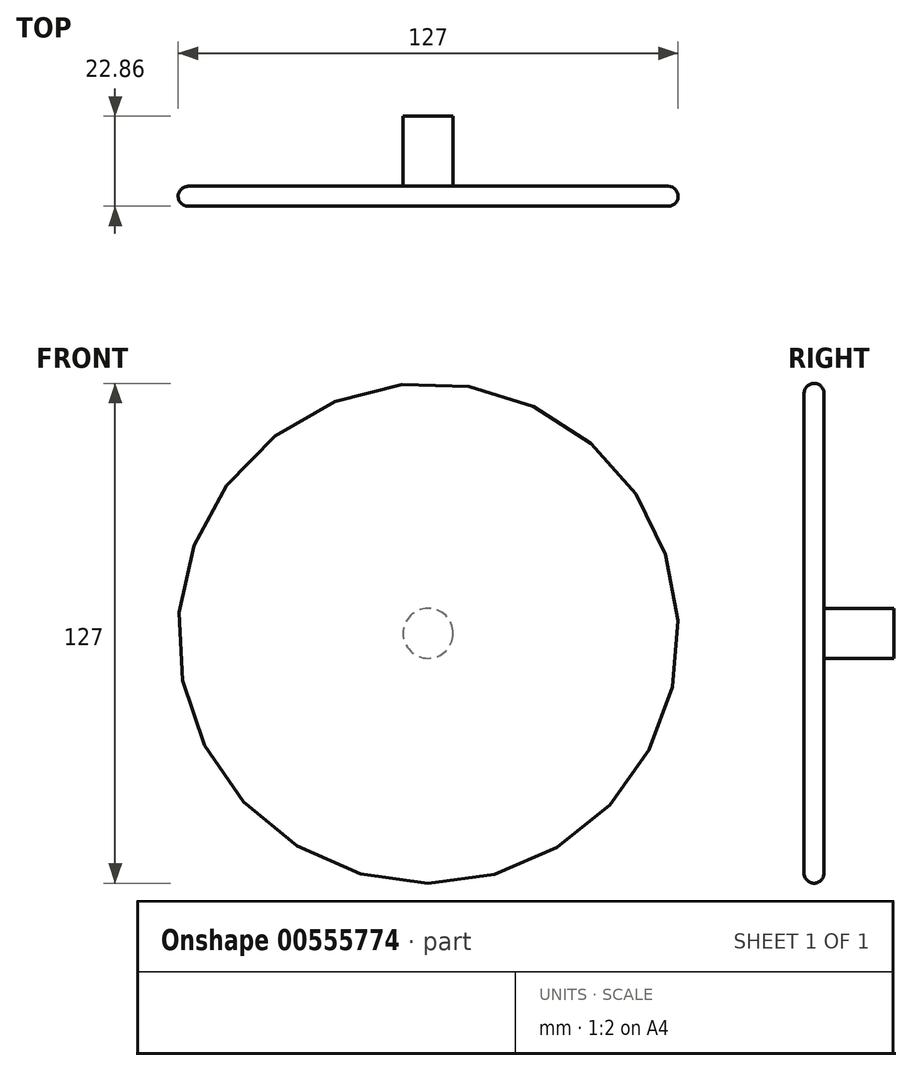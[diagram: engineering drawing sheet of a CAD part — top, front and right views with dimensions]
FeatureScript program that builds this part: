
annotation { "Feature Type Name" : "Feature", "Feature Type Description" : "" }
export const myFeature = defineFeature(function(context is Context, id is Id, definition is map)
    precondition{}
    {
        {
            var Q0;
            Q0=qCreatedBy(makeId("Front.planeOp"),FACE);
            var sketch = newSketch(context, id + "F0", { "sketchPlane" : qUnion([Q0])});
            skCircle(sketch, "E0", {"center": v(0, 0) * mm, "radius": 6.35 * mm});
            skSolve(sketch);
        }
        {
            var Q0;
            Q0=makeQuery(id+"F0.imprint","IMPRINT",FACE,{"disambiguationData":[TD([[makeQuery(id+"F0.imprint","IMPRINT",EDGE,{"derivedFrom":sQuery(id+"F0.wireOp",EDGE,"E0")}),1.0]])]});
            extrude(context, id + "F1", {"entities" : qUnion([Q0]), "depth" : 25.4 * mm, "offsetDistance" : 25.4 * mm});
        }
        {
            var Q0;
            Q0=makeQuery(id+"F1.opExtrude","CAP_FACE",FACE,{"disambiguationData":[OSD([sQuery(id+"F0.wireOp",EDGE,"E0")])],"isStart":false});
            var sketch = newSketch(context, id + "F2", { "sketchPlane" : qUnion([Q0])});
            skCircle(sketch, "E1", {"center": v(0, 0) * mm, "radius": 63.5 * mm});
            skSolve(sketch);
        }
        {
            var Q0;
            Q0=makeQuery(id+"F2.imprint","IMPRINT",FACE,{"disambiguationData":[TD([[makeQuery(id+"F2.imprint","IMPRINT",EDGE,{"derivedFrom":sQuery(id+"F2.wireOp",EDGE,"E1")}),1.0]])]});
            extrude(context, id + "F3", {"entities" : qUnion([Q0]), "operationType" : NewBodyOperationType.ADD, "oppositeDirection" : true, "depth" : 5.08 * mm, "offsetDistance" : 25.4 * mm});
        }
        {
            var Q0;
            Q0=makeQuery(id+"F3.opExtrude","CAP_EDGE",EDGE,{"disambiguationData":[OSD([sQuery(id+"F2.wireOp",EDGE,"E1")])],"isStart":true});
            var Q1;
            Q1=makeQuery(id+"F3.opExtrude","CAP_EDGE",EDGE,{"disambiguationData":[OSD([sQuery(id+"F2.wireOp",EDGE,"E1")])],"isStart":false});
            fillet(context, id + "F4", {"entities" : qUnion([Q0, Q1]), "radius" : 2.54 * mm, "tangentPropagation" : true, "allowEdgeOverflow" : false});
        }
        {
            var Q0;
            Q0=makeQuery(id+"F1.opExtrude","CAP_FACE",FACE,{"disambiguationData":[OSD([sQuery(id+"F0.wireOp",EDGE,"E0")])],"isStart":true});
            extrude(context, id + "F5", {"entities" : qUnion([Q0]), "operationType" : NewBodyOperationType.REMOVE, "oppositeDirection" : true, "depth" : 2.54 * mm, "offsetDistance" : 25.4 * mm});
        }
    });
